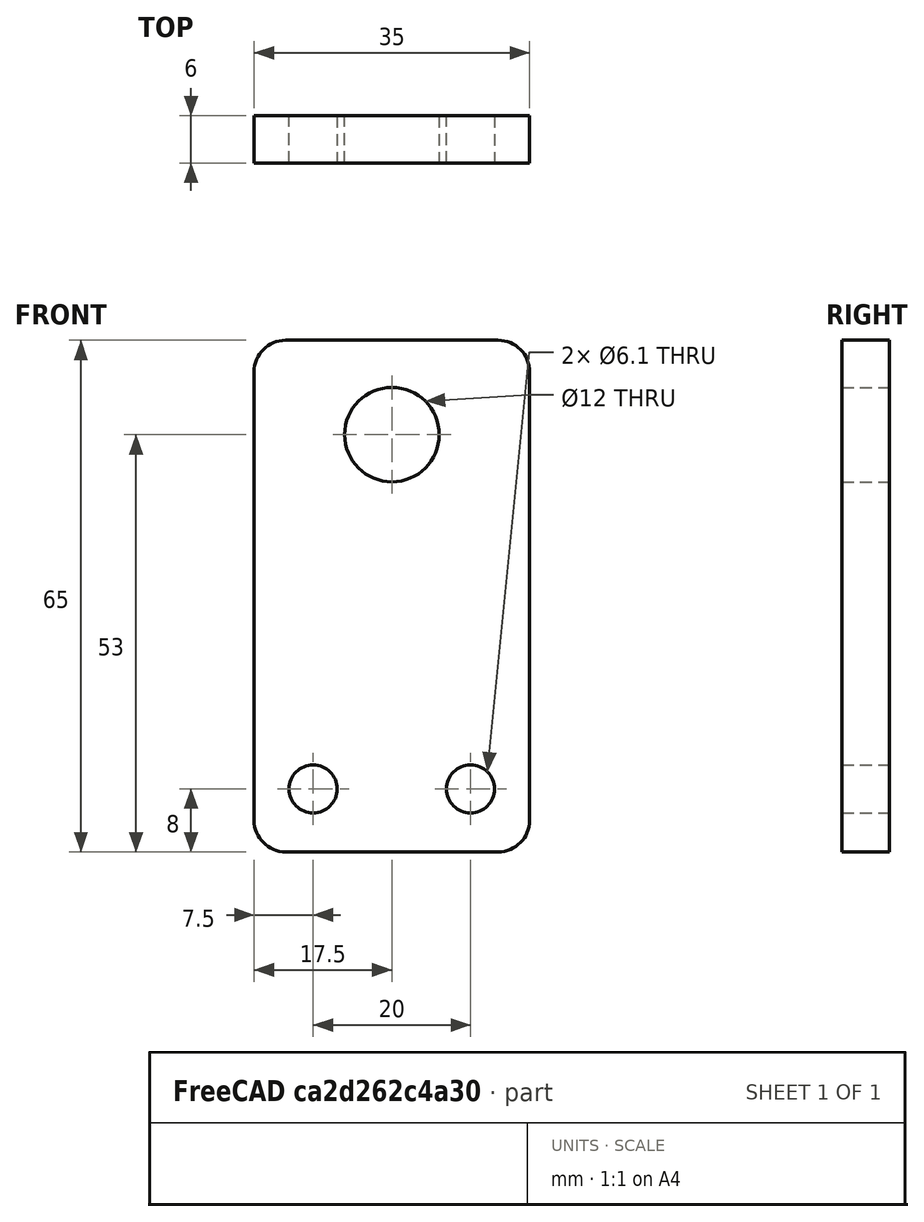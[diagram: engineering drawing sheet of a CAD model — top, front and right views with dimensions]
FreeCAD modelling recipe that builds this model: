
FCSTD DOCUMENT  (FreeCAD 0.15R4671 (Git))
Label: Plaque_support_G
License: All rights reserved
LicenseURL: http://en.wikipedia.org/wiki/All_rights_reserved
objects: Sketcher::SketchObject×1, PartDesign::Pad×1
note: 3 computed .brp shape members not serialized (recipe doc carries the construction recipe); baked Part::Feature solids carry a one-line shape summary decoded from their .brp

FEATURE [Sketcher::SketchObject] Sketch
  Placement = pos=(0,0,0) rot=(1,0,0;1.5708rad)
  sketch-geometry (11):
    g0: Circle CenterX=0 CenterY=0 CenterZ=0 NormalX=0 NormalY=0 NormalZ=1 Radius=6
    g1: Circle CenterX=-10 CenterY=-45 CenterZ=0 NormalX=0 NormalY=0 NormalZ=1 Radius=3.05
    g2: Circle CenterX=10 CenterY=-45 CenterZ=0 NormalX=0 NormalY=0 NormalZ=1 Radius=3.05
    g3: LineSegment StartX=-17.5 StartY=7.99998 StartZ=0 EndX=-17.5 EndY=-49 EndZ=0
    g4: ArcOfCircle CenterX=-13.5 CenterY=-49 CenterZ=0 NormalX=0 NormalY=0 NormalZ=1 Radius=4 StartAngle=3.14159 EndAngle=4.71239
    g5: LineSegment StartX=-13.5 StartY=-53 StartZ=0 EndX=13.5 EndY=-53 EndZ=0
    g6: ArcOfCircle CenterX=13.5 CenterY=-49 CenterZ=0 NormalX=0 NormalY=0 NormalZ=1 Radius=4 StartAngle=4.71239 EndAngle=6.28319
    g7: LineSegment StartX=17.5 StartY=-49 StartZ=0 EndX=17.5 EndY=8 EndZ=0
    g8: ArcOfCircle CenterX=13.5 CenterY=8 CenterZ=0 NormalX=0 NormalY=0 NormalZ=1 Radius=4 StartAngle=0 EndAngle=1.5708
    g9: LineSegment StartX=13.5 StartY=12 StartZ=0 EndX=-13.5 EndY=12 EndZ=0
    g10: ArcOfCircle CenterX=-13.5 CenterY=8 CenterZ=0 NormalX=0 NormalY=0 NormalZ=1 Radius=4 StartAngle=1.5708 EndAngle=3.1416
  constraints (28):
    c: Coincident(g0,g-1)
    c: Radius(g0) = 6
    c: Radius(g1) = 3.05
    c: Equal(g1,g2)
    c: DistanceX(g1,g2) = 20
    c: Symmetric(g1,g2,g-2)
    c: DistanceY(g-1,g1) = -45
    c: Vertical(g3)
    c: Tangent(g3,g4) = -1.5708
    c: Tangent(g4,g5) = -1.5708
    c: Tangent(g5,g6) = -1.5708
    c: Tangent(g6,g7) = -1.5708
    c: Tangent(g7,g8) = -1.5708
    c: Tangent(g8,g9) = -1.5708
    c: Tangent(g9,g10) = -1.5708
    c: Coincident(g10,g3)
    c: Tangent(g3,g10)
    c: Horizontal(g9)
    c: Horizontal(g5)
    c: Vertical(g7)
    c: Radius(g10) = 4
    c: Equal(g10,g8)
    c: Equal(g10,g6)
    c: Equal(g10,g4)
    c: DistanceY(g-1,g9) = 12
    c: Symmetric(g3,g7,g-2)
    c: DistanceY(g1,g4) = -8
    c: DistanceX(g3,g7) = 35
FEATURE [PartDesign::Pad] Pad
  Length = 6
  Length2 = 100
  Placement = pos=(0,0,0) rot=(1,0,0;1.5708rad)
  Sketch = -> Sketch
  Type = 0
